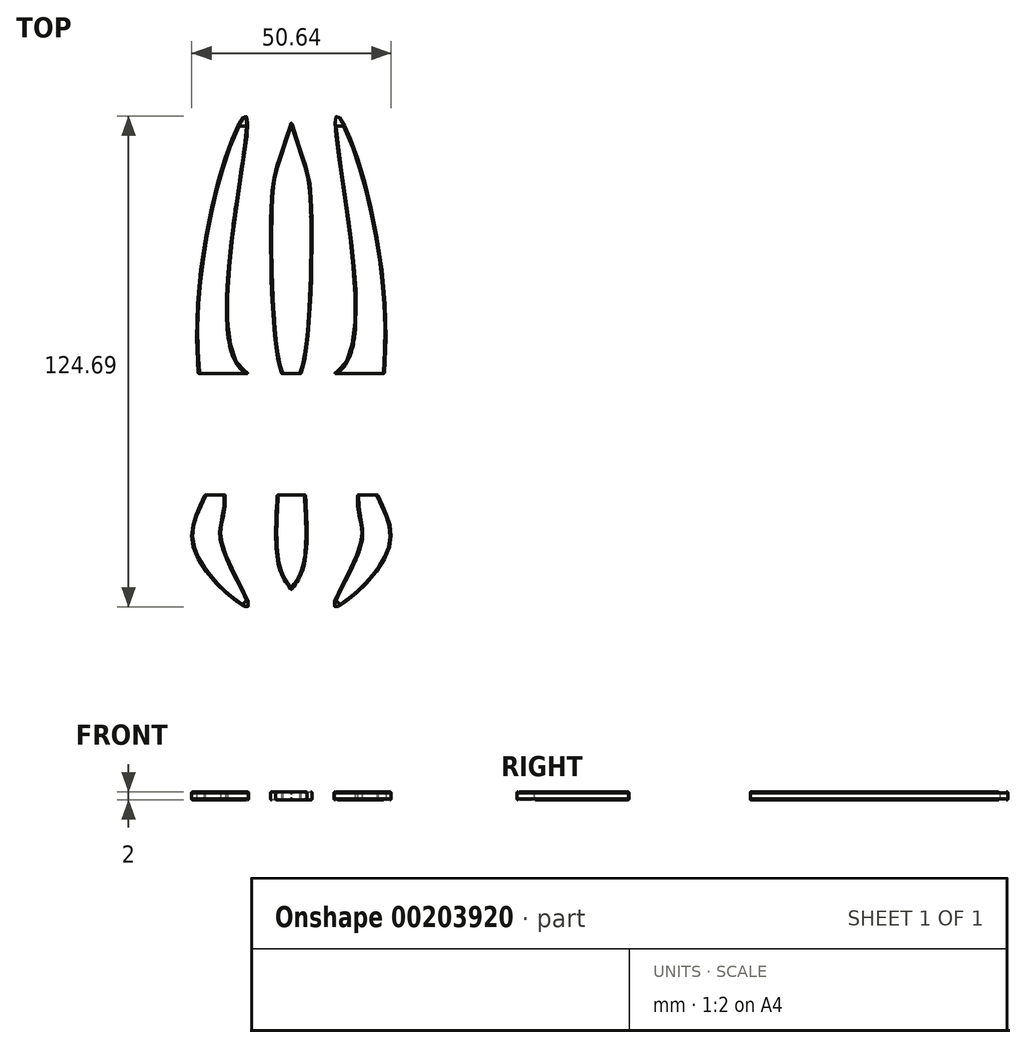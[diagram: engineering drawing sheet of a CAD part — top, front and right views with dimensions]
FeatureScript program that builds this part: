
annotation { "Feature Type Name" : "Feature", "Feature Type Description" : "" }
export const myFeature = defineFeature(function(context is Context, id is Id, definition is map)
    precondition{}
    {
        {
            var Q0;
            Q0=qCreatedBy(makeId("Top.planeOp"),FACE);
            var sketch = newSketch(context, id + "F0", { "sketchPlane" : qUnion([Q0])});
            skFitSpline(sketch, "E0", {"points": [v(-23.61, 9.83) * mm, v(-11.12, 74.15) * mm, v(-10.15, 9.83) * mm], "startDerivative": vector(-18.66, 203.9) * mm, "endDerivative": vector(81.17, -15.6) * mm});
            skLineSegment(sketch, "E1", {"start": v(0, 80.54) * mm, "end": v(0, -51.11) * mm, "construction": true});
            skLineSegment(sketch, "E2", {"start": v(34, 9.83) * mm, "end": v(-34, 9.83) * mm, "construction": true});
            skFitSpline(sketch, "E3", {"points": [v(2.44, 9.83) * mm, v(5.1, 53.39) * mm, v(0, 73.85) * mm], "startDerivative": vector(13.25, 28.7) * mm, "endDerivative": vector(-28.42, 91.52) * mm});
            skFitSpline(sketch, "E4.MirrorCS", {"points": [v(-2.44, 9.83) * mm, v(-5.1, 53.39) * mm, v(0, 73.85) * mm], "startDerivative": vector(-13.25, 28.7) * mm, "endDerivative": vector(28.42, 91.52) * mm});
            skFitSpline(sketch, "E5.MirrorCS", {"points": [v(23.61, 9.83) * mm, v(11.12, 74.15) * mm, v(10.15, 9.83) * mm], "startDerivative": vector(18.66, 203.9) * mm, "endDerivative": vector(-81.17, -15.6) * mm});
            skLineSegment(sketch, "E6", {"start": v(10.15, 9.83) * mm, "end": v(23.61, 9.83) * mm});
            skLineSegment(sketch, "E7", {"start": v(2.44, 9.83) * mm, "end": v(-2.44, 9.83) * mm});
            skLineSegment(sketch, "E8", {"start": v(-10.15, 9.83) * mm, "end": v(-23.61, 9.83) * mm});
            skLineSegment(sketch, "E9", {"start": v(-34, -20.97) * mm, "end": v(34, -20.97) * mm, "construction": true});
            skFitSpline(sketch, "E10", {"points": [v(-21.94, -20.97) * mm, v(-24.3, -36.05) * mm, v(-11, -49.34) * mm, v(-17.59, -33.3) * mm, v(-16.82, -20.97) * mm], "startDerivative": vector(-26.32, -57.17) * mm, "endDerivative": vector(-5.97, 70.05) * mm});
            skFitSpline(sketch, "E11", {"points": [v(-3.6, -20.97) * mm, v(-3.22, -39) * mm, v(0, -45.1) * mm], "startDerivative": vector(-1.8, -33.25) * mm, "endDerivative": vector(9.93, -13.46) * mm});
            skFitSpline(sketch, "E12.MirrorCS", {"points": [v(3.6, -20.97) * mm, v(3.22, -39) * mm, v(0, -45.1) * mm], "startDerivative": vector(1.8, -33.25) * mm, "endDerivative": vector(-9.93, -13.46) * mm});
            skFitSpline(sketch, "E13.MirrorCS", {"points": [v(21.94, -20.97) * mm, v(24.3, -36.05) * mm, v(11, -49.34) * mm, v(17.59, -33.3) * mm, v(16.82, -20.97) * mm], "startDerivative": vector(26.32, -57.17) * mm, "endDerivative": vector(5.97, 70.05) * mm});
            skLineSegment(sketch, "E14", {"start": v(21.94, -20.97) * mm, "end": v(16.82, -20.97) * mm});
            skLineSegment(sketch, "E15", {"start": v(3.6, -20.97) * mm, "end": v(-3.6, -20.97) * mm});
            skLineSegment(sketch, "E16", {"start": v(-16.82, -20.97) * mm, "end": v(-21.94, -20.97) * mm});
            skSolve(sketch);
        }
        {
            var Q0;
            Q0=makeQuery(id+"F0.imprint","IMPRINT",FACE,{"disambiguationData":[TD([[makeQuery(id+"F0.imprint","IMPRINT",EDGE,{"derivedFrom":sQuery(id+"F0.wireOp",EDGE,"E0")}),-1.0]])]});
            var Q1;
            Q1=makeQuery(id+"F0.imprint","IMPRINT",FACE,{"disambiguationData":[TD([[makeQuery(id+"F0.imprint","IMPRINT",EDGE,{"derivedFrom":sQuery(id+"F0.wireOp",EDGE,"E3")}),1.0]])]});
            var Q2;
            Q2=makeQuery(id+"F0.imprint","IMPRINT",FACE,{"disambiguationData":[TD([[makeQuery(id+"F0.imprint","IMPRINT",EDGE,{"derivedFrom":sQuery(id+"F0.wireOp",EDGE,"E5.MirrorCS")}),1.0]])]});
            var Q3;
            Q3=makeQuery(id+"F0.imprint","IMPRINT",FACE,{"disambiguationData":[TD([[makeQuery(id+"F0.imprint","IMPRINT",EDGE,{"derivedFrom":sQuery(id+"F0.wireOp",EDGE,"E13.MirrorCS")}),-1.0]])]});
            var Q4;
            Q4=makeQuery(id+"F0.imprint","IMPRINT",FACE,{"disambiguationData":[TD([[makeQuery(id+"F0.imprint","IMPRINT",EDGE,{"derivedFrom":sQuery(id+"F0.wireOp",EDGE,"E11")}),1.0]])]});
            var Q5;
            Q5=makeQuery(id+"F0.imprint","IMPRINT",FACE,{"disambiguationData":[TD([[makeQuery(id+"F0.imprint","IMPRINT",EDGE,{"derivedFrom":sQuery(id+"F0.wireOp",EDGE,"E10")}),1.0]])]});
            extrude(context, id + "F1", {"entities" : qUnion([Q0, Q1, Q2, Q3, Q4, Q5]), "depth" : 2 * mm});
        }
        {
            var Q0;
            Q0=makeQuery(id+"F1.opExtrude","CAP_EDGE",EDGE,{"disambiguationData":[OSD([sQuery(id+"F0.wireOp",EDGE,"E13.MirrorCS")])],"isStart":true});
            var Q1;
            Q1=makeQuery(id+"F1.opExtrude","CAP_EDGE",EDGE,{"disambiguationData":[OSD([sQuery(id+"F0.wireOp",EDGE,"E13.MirrorCS")])],"isStart":false});
            var Q2;
            Q2=makeQuery(id+"F1.opExtrude","CAP_EDGE",EDGE,{"disambiguationData":[OSD([sQuery(id+"F0.wireOp",EDGE,"E11")])],"isStart":false});
            var Q3;
            Q3=makeQuery(id+"F1.opExtrude","CAP_EDGE",EDGE,{"disambiguationData":[OSD([sQuery(id+"F0.wireOp",EDGE,"E12.MirrorCS")])],"isStart":true});
            var Q4;
            Q4=makeQuery(id+"F1.opExtrude","CAP_EDGE",EDGE,{"disambiguationData":[OSD([sQuery(id+"F0.wireOp",EDGE,"E12.MirrorCS")])],"isStart":false});
            var Q5;
            Q5=makeQuery(id+"F1.opExtrude","CAP_EDGE",EDGE,{"disambiguationData":[OSD([sQuery(id+"F0.wireOp",EDGE,"E10")])],"isStart":false});
            var Q6;
            Q6=makeQuery(id+"F1.opExtrude","CAP_EDGE",EDGE,{"disambiguationData":[OSD([sQuery(id+"F0.wireOp",EDGE,"E10")])],"isStart":true});
            var Q7;
            Q7=makeQuery(id+"F1.opExtrude","CAP_EDGE",EDGE,{"disambiguationData":[OSD([sQuery(id+"F0.wireOp",EDGE,"E5.MirrorCS")])],"isStart":true});
            var Q8;
            Q8=makeQuery(id+"F1.opExtrude","CAP_EDGE",EDGE,{"disambiguationData":[OSD([sQuery(id+"F0.wireOp",EDGE,"E5.MirrorCS")])],"isStart":false});
            var Q9;
            Q9=makeQuery(id+"F1.opExtrude","SWEPT_EDGE",EDGE,{"disambiguationData":[OSD([sQuery(id+"F0.wireOp",EDGE,"E3"),sQuery(id+"F0.wireOp",EDGE,"E7")])]});
            var Q10;
            Q10=makeQuery(id+"F1.opExtrude","CAP_EDGE",EDGE,{"disambiguationData":[OSD([sQuery(id+"F0.wireOp",EDGE,"E3")])],"isStart":true});
            var Q11;
            Q11=makeQuery(id+"F1.opExtrude","CAP_EDGE",EDGE,{"disambiguationData":[OSD([sQuery(id+"F0.wireOp",EDGE,"E3")])],"isStart":false});
            var Q12;
            Q12=makeQuery(id+"F1.opExtrude","CAP_EDGE",EDGE,{"disambiguationData":[OSD([sQuery(id+"F0.wireOp",EDGE,"E4.MirrorCS")])],"isStart":false});
            var Q13;
            Q13=makeQuery(id+"F1.opExtrude","CAP_EDGE",EDGE,{"disambiguationData":[OSD([sQuery(id+"F0.wireOp",EDGE,"E0")])],"isStart":true});
            var Q14;
            Q14=makeQuery(id+"F1.opExtrude","CAP_EDGE",EDGE,{"disambiguationData":[OSD([sQuery(id+"F0.wireOp",EDGE,"E0")])],"isStart":false});
            var Q15;
            {var subQ0=sQuery(id+"F0.wireOp",EDGE,"E14");var subQ1=sQuery(id+"F0.wireOp",EDGE,"E13.MirrorCS");Q15=makeQuery(id+"F1.opExtrude","SWEPT_EDGE",EDGE,{"disambiguationData":[OSD([subQ1,subQ0]),TDD([makeQuery(id+"F0.imprint","INTERSECT",VERTEX,{"disambiguationData":[OD(1.0)],"derivedFrom":[subQ1,subQ0]})])]});}
            var Q16;
            {var subQ0=sQuery(id+"F0.wireOp",EDGE,"E14");var subQ1=sQuery(id+"F0.wireOp",EDGE,"E13.MirrorCS");Q16=makeQuery(id+"F1.opExtrude","SWEPT_EDGE",EDGE,{"disambiguationData":[OSD([subQ1,subQ0]),TDD([makeQuery(id+"F0.imprint","INTERSECT",VERTEX,{"disambiguationData":[OD(0.0)],"derivedFrom":[subQ1,subQ0]})])]});}
            var Q17;
            Q17=makeQuery(id+"F1.opExtrude","CAP_EDGE",EDGE,{"disambiguationData":[OSD([sQuery(id+"F0.wireOp",EDGE,"E14")])],"isStart":true});
            var Q18;
            Q18=makeQuery(id+"F1.opExtrude","CAP_EDGE",EDGE,{"disambiguationData":[OSD([sQuery(id+"F0.wireOp",EDGE,"E14")])],"isStart":false});
            var Q19;
            Q19=makeQuery(id+"F1.opExtrude","SWEPT_EDGE",EDGE,{"disambiguationData":[OSD([sQuery(id+"F0.wireOp",EDGE,"E11"),sQuery(id+"F0.wireOp",EDGE,"E15")])]});
            var Q20;
            Q20=makeQuery(id+"F1.opExtrude","SWEPT_EDGE",EDGE,{"disambiguationData":[OSD([sQuery(id+"F0.wireOp",EDGE,"E11"),sQuery(id+"F0.wireOp",EDGE,"E12.MirrorCS")])]});
            var Q21;
            Q21=makeQuery(id+"F1.opExtrude","SWEPT_EDGE",EDGE,{"disambiguationData":[OSD([sQuery(id+"F0.wireOp",EDGE,"E12.MirrorCS"),sQuery(id+"F0.wireOp",EDGE,"E15")])]});
            var Q22;
            Q22=makeQuery(id+"F1.opExtrude","CAP_EDGE",EDGE,{"disambiguationData":[OSD([sQuery(id+"F0.wireOp",EDGE,"E11")])],"isStart":true});
            var Q23;
            Q23=makeQuery(id+"F1.opExtrude","CAP_EDGE",EDGE,{"disambiguationData":[OSD([sQuery(id+"F0.wireOp",EDGE,"E15")])],"isStart":true});
            var Q24;
            Q24=makeQuery(id+"F1.opExtrude","CAP_EDGE",EDGE,{"disambiguationData":[OSD([sQuery(id+"F0.wireOp",EDGE,"E15")])],"isStart":false});
            var Q25;
            {var subQ0=sQuery(id+"F0.wireOp",EDGE,"E16");var subQ1=sQuery(id+"F0.wireOp",EDGE,"E10");Q25=makeQuery(id+"F1.opExtrude","SWEPT_EDGE",EDGE,{"disambiguationData":[OSD([subQ1,subQ0]),TDD([makeQuery(id+"F0.imprint","INTERSECT",VERTEX,{"disambiguationData":[OD(0.0)],"derivedFrom":[subQ1,subQ0]})])]});}
            var Q26;
            {var subQ0=sQuery(id+"F0.wireOp",EDGE,"E16");var subQ1=sQuery(id+"F0.wireOp",EDGE,"E10");Q26=makeQuery(id+"F1.opExtrude","SWEPT_EDGE",EDGE,{"disambiguationData":[OSD([subQ1,subQ0]),TDD([makeQuery(id+"F0.imprint","INTERSECT",VERTEX,{"disambiguationData":[OD(1.0)],"derivedFrom":[subQ1,subQ0]})])]});}
            var Q27;
            {var subQ0=sQuery(id+"F0.wireOp",EDGE,"E6");var subQ1=sQuery(id+"F0.wireOp",EDGE,"E5.MirrorCS");Q27=makeQuery(id+"F1.opExtrude","SWEPT_EDGE",EDGE,{"disambiguationData":[OSD([subQ1,subQ0]),TDD([makeQuery(id+"F0.imprint","INTERSECT",VERTEX,{"disambiguationData":[OD(0.0)],"derivedFrom":[subQ1,subQ0]})])]});}
            var Q28;
            {var subQ0=sQuery(id+"F0.wireOp",EDGE,"E6");var subQ1=sQuery(id+"F0.wireOp",EDGE,"E5.MirrorCS");Q28=makeQuery(id+"F1.opExtrude","SWEPT_EDGE",EDGE,{"disambiguationData":[OSD([subQ1,subQ0]),TDD([makeQuery(id+"F0.imprint","INTERSECT",VERTEX,{"disambiguationData":[OD(1.0)],"derivedFrom":[subQ1,subQ0]})])]});}
            var Q29;
            Q29=makeQuery(id+"F1.opExtrude","CAP_EDGE",EDGE,{"disambiguationData":[OSD([sQuery(id+"F0.wireOp",EDGE,"E6")])],"isStart":true});
            var Q30;
            Q30=makeQuery(id+"F1.opExtrude","CAP_EDGE",EDGE,{"disambiguationData":[OSD([sQuery(id+"F0.wireOp",EDGE,"E6")])],"isStart":false});
            var Q31;
            Q31=makeQuery(id+"F1.opExtrude","SWEPT_EDGE",EDGE,{"disambiguationData":[OSD([sQuery(id+"F0.wireOp",EDGE,"E3"),sQuery(id+"F0.wireOp",EDGE,"E4.MirrorCS")])]});
            var Q32;
            Q32=makeQuery(id+"F1.opExtrude","SWEPT_EDGE",EDGE,{"disambiguationData":[OSD([sQuery(id+"F0.wireOp",EDGE,"E4.MirrorCS"),sQuery(id+"F0.wireOp",EDGE,"E7")])]});
            var Q33;
            Q33=makeQuery(id+"F1.opExtrude","CAP_EDGE",EDGE,{"disambiguationData":[OSD([sQuery(id+"F0.wireOp",EDGE,"E4.MirrorCS")])],"isStart":true});
            var Q34;
            Q34=makeQuery(id+"F1.opExtrude","CAP_EDGE",EDGE,{"disambiguationData":[OSD([sQuery(id+"F0.wireOp",EDGE,"E7")])],"isStart":true});
            var Q35;
            Q35=makeQuery(id+"F1.opExtrude","CAP_EDGE",EDGE,{"disambiguationData":[OSD([sQuery(id+"F0.wireOp",EDGE,"E7")])],"isStart":false});
            var Q36;
            {var subQ0=sQuery(id+"F0.wireOp",EDGE,"E8");var subQ1=sQuery(id+"F0.wireOp",EDGE,"E0");Q36=makeQuery(id+"F1.opExtrude","SWEPT_EDGE",EDGE,{"disambiguationData":[OSD([subQ1,subQ0]),TDD([makeQuery(id+"F0.imprint","INTERSECT",VERTEX,{"disambiguationData":[OD(0.0)],"derivedFrom":[subQ1,subQ0]})])]});}
            var Q37;
            {var subQ0=sQuery(id+"F0.wireOp",EDGE,"E8");var subQ1=sQuery(id+"F0.wireOp",EDGE,"E0");Q37=makeQuery(id+"F1.opExtrude","SWEPT_EDGE",EDGE,{"disambiguationData":[OSD([subQ1,subQ0]),TDD([makeQuery(id+"F0.imprint","INTERSECT",VERTEX,{"disambiguationData":[OD(1.0)],"derivedFrom":[subQ1,subQ0]})])]});}
            var Q38;
            Q38=makeQuery(id+"F1.opExtrude","CAP_EDGE",EDGE,{"disambiguationData":[OSD([sQuery(id+"F0.wireOp",EDGE,"E8")])],"isStart":true});
            var Q39;
            Q39=makeQuery(id+"F1.opExtrude","CAP_EDGE",EDGE,{"disambiguationData":[OSD([sQuery(id+"F0.wireOp",EDGE,"E8")])],"isStart":false});
            var Q40;
            Q40=makeQuery(id+"F1.opExtrude","CAP_EDGE",EDGE,{"disambiguationData":[OSD([sQuery(id+"F0.wireOp",EDGE,"E16")])],"isStart":true});
            var Q41;
            Q41=makeQuery(id+"F1.opExtrude","CAP_EDGE",EDGE,{"disambiguationData":[OSD([sQuery(id+"F0.wireOp",EDGE,"E16")])],"isStart":false});
            fillet(context, id + "F2", {"entities" : qUnion([Q0, Q1, Q2, Q3, Q4, Q5, Q6, Q7, Q8, Q9, Q10, Q11, Q12, Q13, Q14, Q15, Q16, Q17, Q18, Q19, Q20, Q21, Q22, Q23, Q24, Q25, Q26, Q27, Q28, Q29, Q30, Q31, Q32, Q33, Q34, Q35, Q36, Q37, Q38, Q39, Q40, Q41]), "radius" : 0.27 * mm, "tangentPropagation" : true, "rho" : 0.5, "crossSection" : FilletCrossSection.CONIC, "allowEdgeOverflow" : false});
        }
    });
